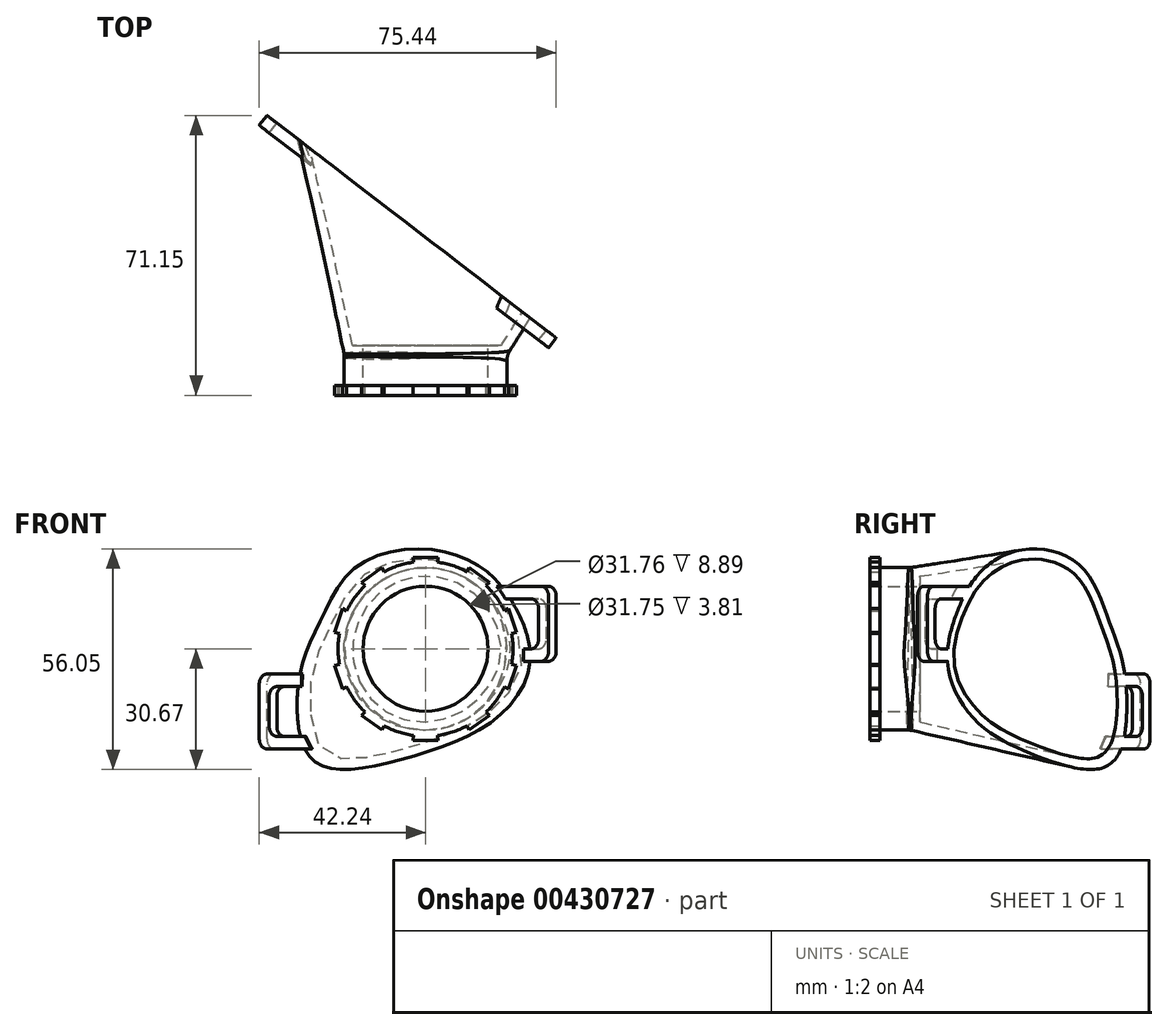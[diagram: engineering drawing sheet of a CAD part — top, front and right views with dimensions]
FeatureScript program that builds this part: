
annotation { "Feature Type Name" : "Feature", "Feature Type Description" : "" }
export const myFeature = defineFeature(function(context is Context, id is Id, definition is map)
    precondition{}
    {
        {
            var Q0;
            Q0=qCreatedBy(makeId("Front.planeOp"),FACE);
            var sketch = newSketch(context, id + "F0", { "sketchPlane" : qUnion([Q0])});
            skCircle(sketch, "E0", {"center": v(0, 0) * mm, "radius": 15.88 * mm});
            skCircle(sketch, "E1.0", {"center": v(0, 0) * mm, "radius": 22.23 * mm});
            skLineSegment(sketch, "E2", {"start": v(0, 0) * mm, "end": v(3.18, 23.22) * mm});
            skLineSegment(sketch, "E3", {"start": v(3.18, 23.22) * mm, "end": v(-3.18, 23.22) * mm});
            skLineSegment(sketch, "E4", {"start": v(-3.18, 23.22) * mm, "end": v(0, 0) * mm});
            skLineSegment(sketch, "E5.1.0", {"start": v(-11.08, 20.65) * mm, "end": v(-16.22, 16.92) * mm});
            skLineSegment(sketch, "E5.1.1", {"start": v(0, 0) * mm, "end": v(-11.08, 20.65) * mm});
            skLineSegment(sketch, "E5.1.2", {"start": v(-16.22, 16.92) * mm, "end": v(0, 0) * mm});
            skLineSegment(sketch, "E5.2.0", {"start": v(-21.1, 10.2) * mm, "end": v(-23.07, 4.16) * mm});
            skLineSegment(sketch, "E5.2.1", {"start": v(0, 0) * mm, "end": v(-21.1, 10.2) * mm});
            skLineSegment(sketch, "E5.2.2", {"start": v(-23.07, 4.16) * mm, "end": v(0, 0) * mm});
            skLineSegment(sketch, "E5.3.0", {"start": v(-23.07, -4.16) * mm, "end": v(-21.1, -10.2) * mm});
            skLineSegment(sketch, "E5.3.1", {"start": v(0, 0) * mm, "end": v(-23.07, -4.16) * mm});
            skLineSegment(sketch, "E5.3.2", {"start": v(-21.1, -10.2) * mm, "end": v(0, 0) * mm});
            skLineSegment(sketch, "E5.4.0", {"start": v(-16.22, -16.92) * mm, "end": v(-11.08, -20.65) * mm});
            skLineSegment(sketch, "E5.4.1", {"start": v(0, 0) * mm, "end": v(-16.22, -16.92) * mm});
            skLineSegment(sketch, "E5.4.2", {"start": v(-11.08, -20.65) * mm, "end": v(0, 0) * mm});
            skLineSegment(sketch, "E5.5.0", {"start": v(-3.18, -23.22) * mm, "end": v(3.17, -23.22) * mm});
            skLineSegment(sketch, "E5.5.1", {"start": v(0, 0) * mm, "end": v(-3.18, -23.22) * mm});
            skLineSegment(sketch, "E5.5.2", {"start": v(3.17, -23.22) * mm, "end": v(0, 0) * mm});
            skLineSegment(sketch, "E5.6.0", {"start": v(11.08, -20.65) * mm, "end": v(16.22, -16.92) * mm});
            skLineSegment(sketch, "E5.6.1", {"start": v(0, 0) * mm, "end": v(11.08, -20.65) * mm});
            skLineSegment(sketch, "E5.6.2", {"start": v(16.22, -16.92) * mm, "end": v(0, 0) * mm});
            skLineSegment(sketch, "E5.7.0", {"start": v(21.1, -10.2) * mm, "end": v(23.07, -4.16) * mm});
            skLineSegment(sketch, "E5.7.1", {"start": v(0, 0) * mm, "end": v(21.1, -10.2) * mm});
            skLineSegment(sketch, "E5.7.2", {"start": v(23.07, -4.16) * mm, "end": v(0, 0) * mm});
            skLineSegment(sketch, "E5.8.0", {"start": v(23.07, 4.16) * mm, "end": v(21.1, 10.2) * mm});
            skLineSegment(sketch, "E5.8.1", {"start": v(0, 0) * mm, "end": v(23.07, 4.16) * mm});
            skLineSegment(sketch, "E5.8.2", {"start": v(21.1, 10.2) * mm, "end": v(0, 0) * mm});
            skLineSegment(sketch, "E5.9.0", {"start": v(16.22, 16.92) * mm, "end": v(11.08, 20.65) * mm});
            skLineSegment(sketch, "E5.9.1", {"start": v(0, 0) * mm, "end": v(16.22, 16.92) * mm});
            skLineSegment(sketch, "E5.9.2", {"start": v(11.08, 20.65) * mm, "end": v(0, 0) * mm});
            skSolve(sketch);
        }
        {
            var Q0;
            Q0=makeQuery(id+"F0.imprint","IMPRINT",FACE,{"disambiguationData":[TD([[makeQuery(id+"F0.imprint","IMPRINT",EDGE,{"derivedFrom":sQuery(id+"F0.wireOp",EDGE,"E0")}),-1.0]])]});
            var Q1;
            {var subQ5=sQuery(id+"F0.wireOp",EDGE,"E5.9.0");Q1=makeQuery(id+"F0.imprint","IMPRINT",FACE,{"disambiguationData":[TD([[makeQuery(id+"F0.imprint","IMPRINT",EDGE,{"derivedFrom":subQ5}),1.0]])]});}
            var Q2;
            {var subQ5=sQuery(id+"F0.wireOp",EDGE,"E5.8.0");Q2=makeQuery(id+"F0.imprint","IMPRINT",FACE,{"disambiguationData":[TD([[makeQuery(id+"F0.imprint","IMPRINT",EDGE,{"derivedFrom":subQ5}),1.0]])]});}
            var Q3;
            {var subQ5=sQuery(id+"F0.wireOp",EDGE,"E5.7.0");Q3=makeQuery(id+"F0.imprint","IMPRINT",FACE,{"disambiguationData":[TD([[makeQuery(id+"F0.imprint","IMPRINT",EDGE,{"derivedFrom":subQ5}),1.0]])]});}
            var Q4;
            {var subQ5=sQuery(id+"F0.wireOp",EDGE,"E5.6.0");Q4=makeQuery(id+"F0.imprint","IMPRINT",FACE,{"disambiguationData":[TD([[makeQuery(id+"F0.imprint","IMPRINT",EDGE,{"derivedFrom":subQ5}),1.0]])]});}
            var Q5;
            {var subQ5=sQuery(id+"F0.wireOp",EDGE,"E3");Q5=makeQuery(id+"F0.imprint","IMPRINT",FACE,{"disambiguationData":[TD([[makeQuery(id+"F0.imprint","IMPRINT",EDGE,{"derivedFrom":subQ5}),1.0]])]});}
            var Q6;
            {var subQ5=sQuery(id+"F0.wireOp",EDGE,"E5.1.0");Q6=makeQuery(id+"F0.imprint","IMPRINT",FACE,{"disambiguationData":[TD([[makeQuery(id+"F0.imprint","IMPRINT",EDGE,{"derivedFrom":subQ5}),1.0]])]});}
            var Q7;
            {var subQ5=sQuery(id+"F0.wireOp",EDGE,"E5.2.0");Q7=makeQuery(id+"F0.imprint","IMPRINT",FACE,{"disambiguationData":[TD([[makeQuery(id+"F0.imprint","IMPRINT",EDGE,{"derivedFrom":subQ5}),1.0]])]});}
            var Q8;
            {var subQ5=sQuery(id+"F0.wireOp",EDGE,"E5.3.0");Q8=makeQuery(id+"F0.imprint","IMPRINT",FACE,{"disambiguationData":[TD([[makeQuery(id+"F0.imprint","IMPRINT",EDGE,{"derivedFrom":subQ5}),1.0]])]});}
            var Q9;
            {var subQ5=sQuery(id+"F0.wireOp",EDGE,"E5.4.0");Q9=makeQuery(id+"F0.imprint","IMPRINT",FACE,{"disambiguationData":[TD([[makeQuery(id+"F0.imprint","IMPRINT",EDGE,{"derivedFrom":subQ5}),1.0]])]});}
            var Q10;
            {var subQ5=sQuery(id+"F0.wireOp",EDGE,"E5.5.0");Q10=makeQuery(id+"F0.imprint","IMPRINT",FACE,{"disambiguationData":[TD([[makeQuery(id+"F0.imprint","IMPRINT",EDGE,{"derivedFrom":subQ5}),1.0]])]});}
            extrude(context, id + "F1", {"entities" : qUnion([Q0, Q1, Q2, Q3, Q4, Q5, Q6, Q7, Q8, Q9, Q10]), "depth" : 2.54 * mm, "offsetDistance" : 25.4 * mm});
        }
        {
            var Q0;
            Q0=qCreatedBy(makeId("Front.planeOp"),FACE);
            var sketch = newSketch(context, id + "F2", { "sketchPlane" : qUnion([Q0])});
            skCircle(sketch, "E6", {"center": v(0, 0) * mm, "radius": 20.64 * mm});
            skCircle(sketch, "E7", {"center": v(0, 0) * mm, "radius": 15.88 * mm});
            skSolve(sketch);
        }
        {
            var Q0;
            Q0=makeQuery(id+"F2.imprint","IMPRINT",FACE,{"disambiguationData":[TD([[makeQuery(id+"F2.imprint","IMPRINT",EDGE,{"derivedFrom":sQuery(id+"F2.wireOp",EDGE,"E6")}),1.0]])]});
            extrude(context, id + "F3", {"entities" : qUnion([Q0]), "operationType" : NewBodyOperationType.ADD, "oppositeDirection" : true, "depth" : 6.35 * mm, "offsetDistance" : 25.4 * mm});
        }
        {
            var Q0;
            Q0=makeQuery(id+"F3.opExtrude","CAP_FACE",FACE,{"disambiguationData":[OSD([sQuery(id+"F2.wireOp",EDGE,"E6"),sQuery(id+"F2.wireOp",EDGE,"E7")])],"isStart":false});
            cPlane(context, id + "F4", {"entities" : qUnion([Q0]), "cplaneType" : CPlaneType.OFFSET, "offset" : 12.7 * mm, "width" : 152.4 * mm, "height" : 152.4 * mm});
        }
        {
            var Q0;
            Q0=makeQuery(id+"F3.opExtrude","CAP_FACE",FACE,{"disambiguationData":[OSD([sQuery(id+"F2.wireOp",EDGE,"E6"),sQuery(id+"F2.wireOp",EDGE,"E7")])],"isStart":false});
            cPlane(context, id + "F5", {"entities" : qUnion([Q0]), "cplaneType" : CPlaneType.OFFSET, "offset" : 50.8 * mm, "width" : 152.4 * mm, "height" : 152.4 * mm});
        }
        {
            var Q0;
            Q0=qCreatedBy(id+"F4.planeOp",FACE);
            var sketch = newSketch(context, id + "F6", { "sketchPlane" : qUnion([Q0])});
            skLineSegment(sketch, "E8", {"start": v(-24.13, 18.2) * mm, "end": v(-24.13, -16.35) * mm});
            skSolve(sketch);
        }
        {
            var Q0;
            Q0=qCreatedBy(id+"F5.planeOp",FACE);
            var sketch = newSketch(context, id + "F7", { "sketchPlane" : qUnion([Q0])});
            skLineSegment(sketch, "E9", {"start": v(25.4, 13.1) * mm, "end": v(25.4, -20.7) * mm});
            skSolve(sketch);
        }
        {
            var Q0;
            Q0=sQuery(id+"F6.wireOp",VERTEX,"E8.start");
            var Q1;
            Q1=sQuery(id+"F6.wireOp",VERTEX,"E8.end");
            var Q2;
            Q2=sQuery(id+"F7.wireOp",VERTEX,"E9.start");
            cPlane(context, id + "F8", {"entities" : qUnion([Q0, Q1, Q2]), "cplaneType" : CPlaneType.THREE_POINT, "offset" : 25.4 * mm, "width" : 152.4 * mm, "height" : 152.4 * mm});
        }
        {
            var Q0;
            Q0=qCreatedBy(id+"F8.planeOp",FACE);
            var sketch = newSketch(context, id + "F9", { "sketchPlane" : qUnion([Q0])});
            skFitSpline(sketch, "E10", {"points": [v(5.5, 11) * mm, v(-3.5, 19.76) * mm, v(-21.72, 25.25) * mm, v(-45.86, 20.37) * mm, v(-56.38, 7.55) * mm, v(-62.29, -3.44) * mm, v(-64.09, -15.24) * mm, v(-61.26, -26.03) * mm, v(-52.27, -30.5) * mm, v(-27.63, -27.45) * mm, v(0, -17.48) * mm, v(10.63, -3.03) * mm, v(5.5, 11) * mm]});
            skSolve(sketch);
        }
        {
            var Q0;
            Q0=makeQuery(id+"F3.opExtrude","CAP_FACE",FACE,{"disambiguationData":[OSD([sQuery(id+"F2.wireOp",EDGE,"E6"),sQuery(id+"F2.wireOp",EDGE,"E7")])],"isStart":false});
            var sketch = newSketch(context, id + "F10", { "sketchPlane" : qUnion([Q0])});
            skCircle(sketch, "E11", {"center": v(0, 0) * mm, "radius": 20.64 * mm});
            skSolve(sketch);
        }
        {
            var Q0;
            Q0 = qSketchRegion(id + "F10", true);
            extrude(context, id + "F11", {"entities" : qUnion([Q0]), "operationType" : NewBodyOperationType.ADD, "depth" : 1.27 * mm, "offsetDistance" : 25.4 * mm});
        }
        {
            var Q0;
            Q0=makeQuery(id+"F9.imprint","IMPRINT",FACE,{"disambiguationData":[TD([[makeQuery(id+"F9.imprint","IMPRINT",EDGE,{"derivedFrom":sQuery(id+"F9.wireOp",EDGE,"E10")}),1.0]])]});
            var Q1;
            Q1=makeQuery(id+"F11.opExtrude","CAP_FACE",FACE,{"disambiguationData":[OSD([sQuery(id+"F10.wireOp",EDGE,"E11")])],"isStart":false});
            loft(context, id + "F12", {"sheetProfilesArray" : [{ "sheetProfileEntities" : qUnion([Q0]) }, { "sheetProfileEntities" : qUnion([Q1]) }]});
        }
        {
            var Q0;
            Q0=makeQuery(id+"F12.opLoft","CAP_FACE",FACE,{"disambiguationData":[OSD([makeQuery(id+"F9.imprint","IMPRINT",FACE,{"disambiguationData":[TD([[makeQuery(id+"F9.imprint","IMPRINT",EDGE,{"derivedFrom":sQuery(id+"F9.wireOp",EDGE,"E10")}),1.0]])]})])],"isStart":true});
            shell(context, id + "F13", {"entities" : qUnion([Q0]), "thickness" : 2.54 * mm});
        }
        {
            var Q0;
            Q0=makeQuery(id+"F1.opExtrude","SWEPT_BODY",BODY,{"disambiguationData":[OSD([sQuery(id+"F0.wireOp",EDGE,"E0"),sQuery(id+"F0.wireOp",EDGE,"E1.0"),sQuery(id+"F0.wireOp",EDGE,"E2"),sQuery(id+"F0.wireOp",EDGE,"E3"),sQuery(id+"F0.wireOp",EDGE,"E4"),sQuery(id+"F0.wireOp",EDGE,"E5.1.0"),sQuery(id+"F0.wireOp",EDGE,"E5.1.1"),sQuery(id+"F0.wireOp",EDGE,"E5.1.2"),sQuery(id+"F0.wireOp",EDGE,"E5.2.0"),sQuery(id+"F0.wireOp",EDGE,"E5.2.1"),sQuery(id+"F0.wireOp",EDGE,"E5.2.2"),sQuery(id+"F0.wireOp",EDGE,"E5.3.0"),sQuery(id+"F0.wireOp",EDGE,"E5.3.1"),sQuery(id+"F0.wireOp",EDGE,"E5.3.2"),sQuery(id+"F0.wireOp",EDGE,"E5.4.0"),sQuery(id+"F0.wireOp",EDGE,"E5.4.1"),sQuery(id+"F0.wireOp",EDGE,"E5.4.2"),sQuery(id+"F0.wireOp",EDGE,"E5.5.0"),sQuery(id+"F0.wireOp",EDGE,"E5.5.1"),sQuery(id+"F0.wireOp",EDGE,"E5.5.2"),sQuery(id+"F0.wireOp",EDGE,"E5.6.0"),sQuery(id+"F0.wireOp",EDGE,"E5.6.1"),sQuery(id+"F0.wireOp",EDGE,"E5.6.2"),sQuery(id+"F0.wireOp",EDGE,"E5.7.0"),sQuery(id+"F0.wireOp",EDGE,"E5.7.1"),sQuery(id+"F0.wireOp",EDGE,"E5.7.2"),sQuery(id+"F0.wireOp",EDGE,"E5.8.0"),sQuery(id+"F0.wireOp",EDGE,"E5.8.1"),sQuery(id+"F0.wireOp",EDGE,"E5.8.2"),sQuery(id+"F0.wireOp",EDGE,"E5.9.0"),sQuery(id+"F0.wireOp",EDGE,"E5.9.1"),sQuery(id+"F0.wireOp",EDGE,"E5.9.2")])]});
            var Q1;
            Q1=makeQuery(id+"F12.opLoft","SWEPT_BODY",BODY,{"disambiguationData":[OSD([makeQuery(id+"F9.imprint","IMPRINT",FACE,{"disambiguationData":[TD([[makeQuery(id+"F9.imprint","IMPRINT",EDGE,{"derivedFrom":sQuery(id+"F9.wireOp",EDGE,"E10")}),1.0]])]}),sQuery(id+"F10.wireOp",EDGE,"E11")])]});
            booleanBodies(context, id + "F14", {"operationType" : BooleanOperationType.UNION, "tools" : qUnion([Q0, Q1])});
        }
        {
            var Q0;
            {var subQ0=sQuery(id+"F10.wireOp",EDGE,"E11");Q0=makeQuery(id+"F14.opBoolean","MERGE",EDGE,{"derivedFrom":[makeQuery(id+"F11.opExtrude","CAP_EDGE",EDGE,{"disambiguationData":[OSD([subQ0])],"isStart":false}),makeQuery(id+"F12.opLoft","MID_CAP_EDGE",EDGE,{"disambiguationData":[OSD([subQ0])],"capPos":1.0})]});}
            fillet(context, id + "F15", {"entities" : qUnion([Q0]), "radius" : 5.08 * mm, "tangentPropagation" : true, "allowEdgeOverflow" : false});
        }
        {
            var Q0;
            Q0=sQuery(id+"F0.wireOp",VERTEX,"E0.center");
            var Q1;
            Q1=makeQuery(id+"F1.opExtrude","SWEPT_BODY",BODY,{"disambiguationData":[OSD([sQuery(id+"F0.wireOp",EDGE,"E0"),sQuery(id+"F0.wireOp",EDGE,"E1.0"),sQuery(id+"F0.wireOp",EDGE,"E2"),sQuery(id+"F0.wireOp",EDGE,"E3"),sQuery(id+"F0.wireOp",EDGE,"E4"),sQuery(id+"F0.wireOp",EDGE,"E5.1.0"),sQuery(id+"F0.wireOp",EDGE,"E5.1.1"),sQuery(id+"F0.wireOp",EDGE,"E5.1.2"),sQuery(id+"F0.wireOp",EDGE,"E5.2.0"),sQuery(id+"F0.wireOp",EDGE,"E5.2.1"),sQuery(id+"F0.wireOp",EDGE,"E5.2.2"),sQuery(id+"F0.wireOp",EDGE,"E5.3.0"),sQuery(id+"F0.wireOp",EDGE,"E5.3.1"),sQuery(id+"F0.wireOp",EDGE,"E5.3.2"),sQuery(id+"F0.wireOp",EDGE,"E5.4.0"),sQuery(id+"F0.wireOp",EDGE,"E5.4.1"),sQuery(id+"F0.wireOp",EDGE,"E5.4.2"),sQuery(id+"F0.wireOp",EDGE,"E5.5.0"),sQuery(id+"F0.wireOp",EDGE,"E5.5.1"),sQuery(id+"F0.wireOp",EDGE,"E5.5.2"),sQuery(id+"F0.wireOp",EDGE,"E5.6.0"),sQuery(id+"F0.wireOp",EDGE,"E5.6.1"),sQuery(id+"F0.wireOp",EDGE,"E5.6.2"),sQuery(id+"F0.wireOp",EDGE,"E5.7.0"),sQuery(id+"F0.wireOp",EDGE,"E5.7.1"),sQuery(id+"F0.wireOp",EDGE,"E5.7.2"),sQuery(id+"F0.wireOp",EDGE,"E5.8.0"),sQuery(id+"F0.wireOp",EDGE,"E5.8.1"),sQuery(id+"F0.wireOp",EDGE,"E5.8.2"),sQuery(id+"F0.wireOp",EDGE,"E5.9.0"),sQuery(id+"F0.wireOp",EDGE,"E5.9.1"),sQuery(id+"F0.wireOp",EDGE,"E5.9.2")])]});
            hole(context, id + "F16", {"style" : HoleStyle.SIMPLE, "endStyle" : HoleEndStyle.BLIND, "holeDiameter" : 31.75 * mm, "majorDiameter" : 6.35 * mm, "holeDepth" : 19.05 * mm, "isTappedThrough" : true, "tappedDepth" : 12.7 * mm, "tapClearance" : 3, "locations" : qUnion([Q0]), "scope" : qUnion([Q1]), "startStyle" : HoleStartStyle.PART});
        }
        {
            var Q0;
            Q0=qCreatedBy(id+"F8.planeOp",FACE);
            var sketch = newSketch(context, id + "F17", { "sketchPlane" : qUnion([Q0])});
            skLineSegment(sketch, "E12", {"start": v(-61.65, -25.44) * mm, "end": v(-73.78, -25.44) * mm});
            skLineSegment(sketch, "E13", {"start": v(-73.78, -25.44) * mm, "end": v(-73.78, -6.4) * mm});
            skLineSegment(sketch, "E14", {"start": v(-73.78, -6.4) * mm, "end": v(-63.2, -6.4) * mm});
            skLineSegment(sketch, "E15", {"start": v(-63.8, -9.57) * mm, "end": v(-70.6, -9.57) * mm});
            skLineSegment(sketch, "E16", {"start": v(-70.6, -9.57) * mm, "end": v(-70.6, -22.27) * mm});
            skLineSegment(sketch, "E17", {"start": v(-70.6, -22.27) * mm, "end": v(-63.06, -22.27) * mm});
            skLineSegment(sketch, "E18", {"start": v(1.46, 15.88) * mm, "end": v(18.96, 15.88) * mm});
            skLineSegment(sketch, "E19", {"start": v(18.96, 15.88) * mm, "end": v(18.96, -3.17) * mm});
            skLineSegment(sketch, "E20", {"start": v(18.96, -3.17) * mm, "end": v(10.62, -3.18) * mm});
            skLineSegment(sketch, "E21", {"start": v(10.52, 0) * mm, "end": v(15.78, 0) * mm});
            skLineSegment(sketch, "E22", {"start": v(15.78, 0) * mm, "end": v(15.78, 12.7) * mm});
            skLineSegment(sketch, "E23", {"start": v(15.78, 12.7) * mm, "end": v(4.25, 12.7) * mm});
            skLineSegment(sketch, "E24", {"start": v(4.25, 12.7) * mm, "end": v(2.2, 12.7) * mm});
            skLineSegment(sketch, "E25", {"start": v(2.2, 12.7) * mm, "end": v(0, 15.88) * mm});
            skLineSegment(sketch, "E26", {"start": v(0, 15.88) * mm, "end": v(1.46, 15.88) * mm});
            skLineSegment(sketch, "E27", {"start": v(10.52, 0) * mm, "end": v(8.72, 0) * mm});
            skLineSegment(sketch, "E28", {"start": v(8.72, 0) * mm, "end": v(8.72, -3.18) * mm});
            skLineSegment(sketch, "E29", {"start": v(8.72, -3.18) * mm, "end": v(10.62, -3.18) * mm});
            skLineSegment(sketch, "E30", {"start": v(-63.2, -6.4) * mm, "end": v(-60.22, -6.4) * mm});
            skLineSegment(sketch, "E31", {"start": v(-60.22, -6.4) * mm, "end": v(-60.22, -9.57) * mm});
            skLineSegment(sketch, "E32", {"start": v(-60.22, -9.57) * mm, "end": v(-63.8, -9.57) * mm});
            skLineSegment(sketch, "E33", {"start": v(-63.06, -22.27) * mm, "end": v(-59.13, -22.27) * mm});
            skLineSegment(sketch, "E34", {"start": v(-57, -25.44) * mm, "end": v(-61.65, -25.44) * mm});
            skLineSegment(sketch, "E35", {"start": v(-59.13, -22.27) * mm, "end": v(-57, -25.44) * mm});
            skSolve(sketch);
        }
        {
            var Q0;
            Q0=makeQuery(id+"F17.imprint","IMPRINT",FACE,{"disambiguationData":[TD([[makeQuery(id+"F17.imprint","IMPRINT",EDGE,{"derivedFrom":sQuery(id+"F17.wireOp",EDGE,"E18")}),-1.0]])]});
            var Q1;
            Q1=makeQuery(id+"F17.imprint","IMPRINT",FACE,{"disambiguationData":[TD([[makeQuery(id+"F17.imprint","IMPRINT",EDGE,{"derivedFrom":sQuery(id+"F17.wireOp",EDGE,"E12")}),-1.0]])]});
            extrude(context, id + "F18", {"entities" : qUnion([Q0, Q1]), "operationType" : NewBodyOperationType.ADD, "depth" : 3.17 * mm, "offsetDistance" : 25.4 * mm});
        }
        {
            var Q0;
            Q0=makeQuery(id+"F18.opExtrude","SWEPT_EDGE",EDGE,{"disambiguationData":[OSD([sQuery(id+"F17.wireOp",EDGE,"E34"),sQuery(id+"F17.wireOp",EDGE,"E35")])]});
            var Q1;
            Q1=makeQuery(id+"F18.opExtrude","SWEPT_EDGE",EDGE,{"disambiguationData":[OSD([sQuery(id+"F17.wireOp",EDGE,"E33"),sQuery(id+"F17.wireOp",EDGE,"E35")])]});
            fillet(context, id + "F19", {"entities" : qUnion([Q0, Q1]), "radius" : 0.25 * mm, "tangentPropagation" : true, "allowEdgeOverflow" : false});
        }
        {
            var Q0;
            Q0=makeQuery(id+"F18.opExtrude","SWEPT_EDGE",EDGE,{"disambiguationData":[OSD([sQuery(id+"F17.wireOp",EDGE,"E18"),sQuery(id+"F17.wireOp",EDGE,"E19")])]});
            var Q1;
            Q1=makeQuery(id+"F18.opExtrude","SWEPT_EDGE",EDGE,{"disambiguationData":[OSD([sQuery(id+"F17.wireOp",EDGE,"E19"),sQuery(id+"F17.wireOp",EDGE,"E20")])]});
            var Q2;
            Q2=makeQuery(id+"F18.opExtrude","SWEPT_EDGE",EDGE,{"disambiguationData":[OSD([sQuery(id+"F17.wireOp",EDGE,"E13"),sQuery(id+"F17.wireOp",EDGE,"E14")])]});
            var Q3;
            Q3=makeQuery(id+"F18.opExtrude","SWEPT_EDGE",EDGE,{"disambiguationData":[OSD([sQuery(id+"F17.wireOp",EDGE,"E12"),sQuery(id+"F17.wireOp",EDGE,"E13")])]});
            var Q4;
            Q4=makeQuery(id+"F18.opExtrude","SWEPT_EDGE",EDGE,{"disambiguationData":[OSD([sQuery(id+"F17.wireOp",EDGE,"E15"),sQuery(id+"F17.wireOp",EDGE,"E16")])]});
            var Q5;
            Q5=makeQuery(id+"F18.opExtrude","SWEPT_EDGE",EDGE,{"disambiguationData":[OSD([sQuery(id+"F17.wireOp",EDGE,"E16"),sQuery(id+"F17.wireOp",EDGE,"E17")])]});
            var Q6;
            Q6=makeQuery(id+"F18.opExtrude","SWEPT_EDGE",EDGE,{"disambiguationData":[OSD([sQuery(id+"F17.wireOp",EDGE,"E21"),sQuery(id+"F17.wireOp",EDGE,"E22")])]});
            var Q7;
            Q7=makeQuery(id+"F18.opExtrude","SWEPT_EDGE",EDGE,{"disambiguationData":[OSD([sQuery(id+"F17.wireOp",EDGE,"E22"),sQuery(id+"F17.wireOp",EDGE,"E23")])]});
            fillet(context, id + "F20", {"entities" : qUnion([Q0, Q1, Q2, Q3, Q4, Q5, Q6, Q7]), "radius" : 2.54 * mm, "tangentPropagation" : true, "allowEdgeOverflow" : false});
        }
    });
